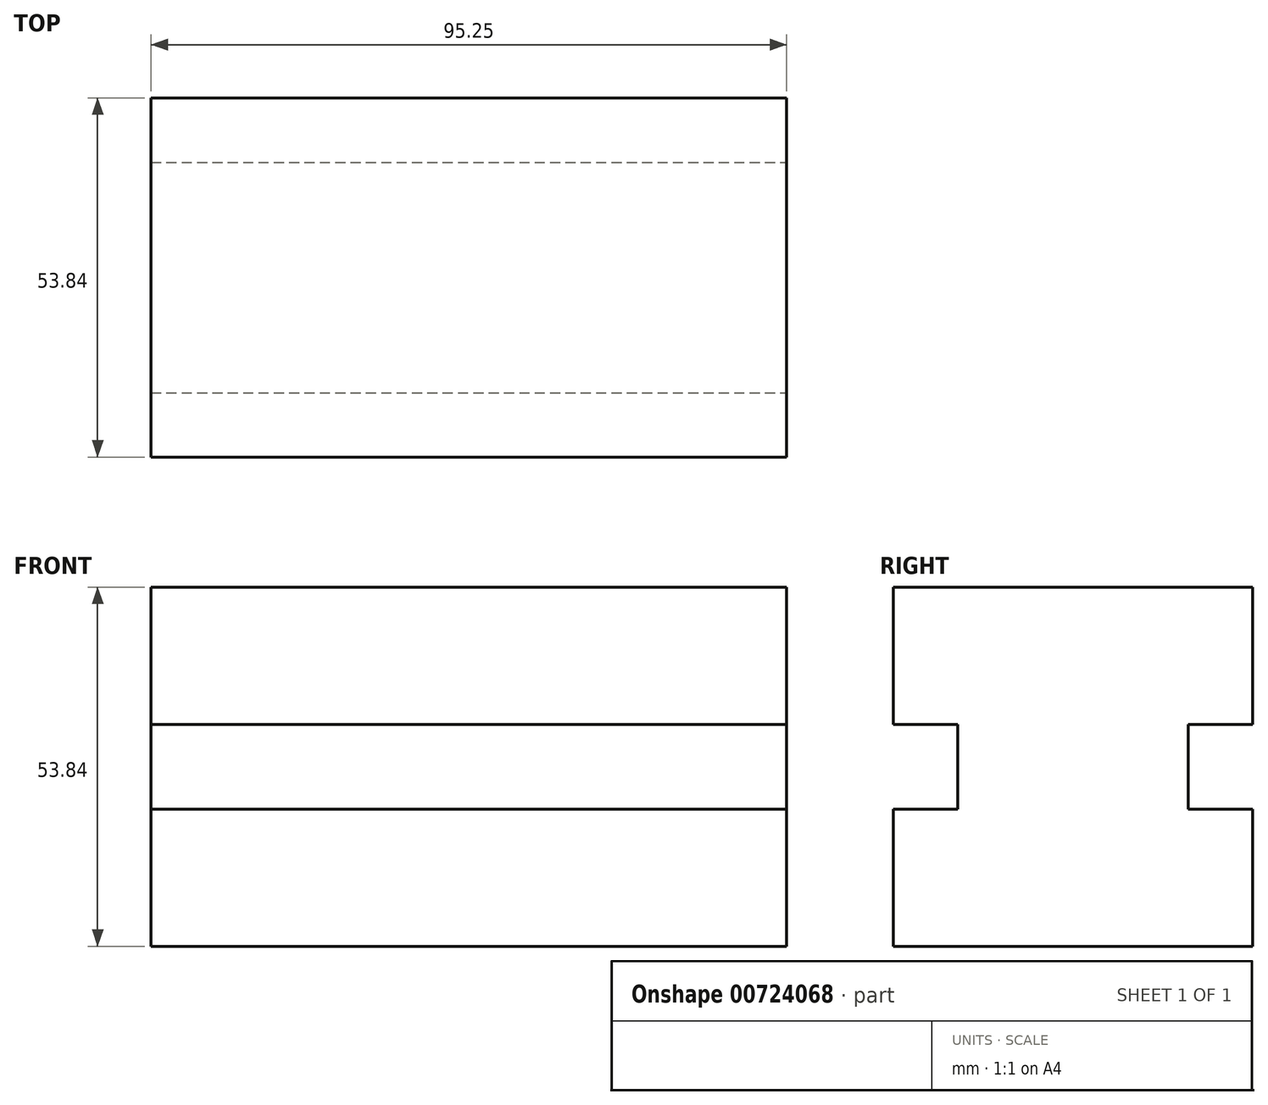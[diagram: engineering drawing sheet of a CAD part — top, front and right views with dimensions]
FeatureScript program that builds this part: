
annotation { "Feature Type Name" : "Feature", "Feature Type Description" : "" }
export const myFeature = defineFeature(function(context is Context, id is Id, definition is map)
    precondition{}
    {
        {
            var Q0;
            Q0=qCreatedBy(makeId("Right.planeOp"),FACE);
            var sketch = newSketch(context, id + "F0", { "sketchPlane" : qUnion([Q0])});
            skLineSegment(sketch, "E0.bottom", {"start": v(26.92, -26.92) * mm, "end": v(-26.92, -26.92) * mm});
            skLineSegment(sketch, "E0.top", {"start": v(26.92, 26.92) * mm, "end": v(-26.92, 26.92) * mm});
            skLineSegment(sketch, "E0.left", {"start": v(26.92, -26.92) * mm, "end": v(26.92, -6.35) * mm});
            skLineSegment(sketch, "E0.right", {"start": v(-26.92, -26.92) * mm, "end": v(-26.92, -6.35) * mm});
            skPoint(sketch, "E0.middle", {"position": v(0, 0) * mm});
            skLineSegment(sketch, "E1.bottom", {"start": v(-26.92, 6.35) * mm, "end": v(-17.27, 6.35) * mm});
            skLineSegment(sketch, "E1.top", {"start": v(-26.92, -6.35) * mm, "end": v(-17.27, -6.35) * mm});
            skLineSegment(sketch, "E1.right", {"start": v(-17.27, 6.35) * mm, "end": v(-17.27, -6.35) * mm});
            skPoint(sketch, "E2.firstSnap0", {"position": v(-22.1, 6.35) * mm});
            skLineSegment(sketch, "E2.bottom", {"start": v(26.92, 6.35) * mm, "end": v(17.27, 6.35) * mm});
            skLineSegment(sketch, "E2.top", {"start": v(26.92, -6.35) * mm, "end": v(17.27, -6.35) * mm});
            skLineSegment(sketch, "E2.right", {"start": v(17.27, 6.35) * mm, "end": v(17.27, -6.35) * mm});
            skLineSegment(sketch, "E3.trimOffspring", {"start": v(-26.92, 6.35) * mm, "end": v(-26.92, 26.92) * mm});
            skLineSegment(sketch, "E4.trimOffspring", {"start": v(26.92, 6.35) * mm, "end": v(26.92, 26.92) * mm});
            skSolve(sketch);
        }
        {
            var Q0;
            Q0=makeQuery(id+"F0.imprint","IMPRINT",FACE,{"disambiguationData":[TD([[makeQuery(id+"F0.imprint","IMPRINT",EDGE,{"derivedFrom":sQuery(id+"F0.wireOp",EDGE,"E0.bottom")}),-1.0]])]});
            extrude(context, id + "F1", {"entities" : qUnion([Q0]), "oppositeDirection" : true, "depth" : 95.25 * mm, "offsetDistance" : 25.4 * mm});
        }
    });
